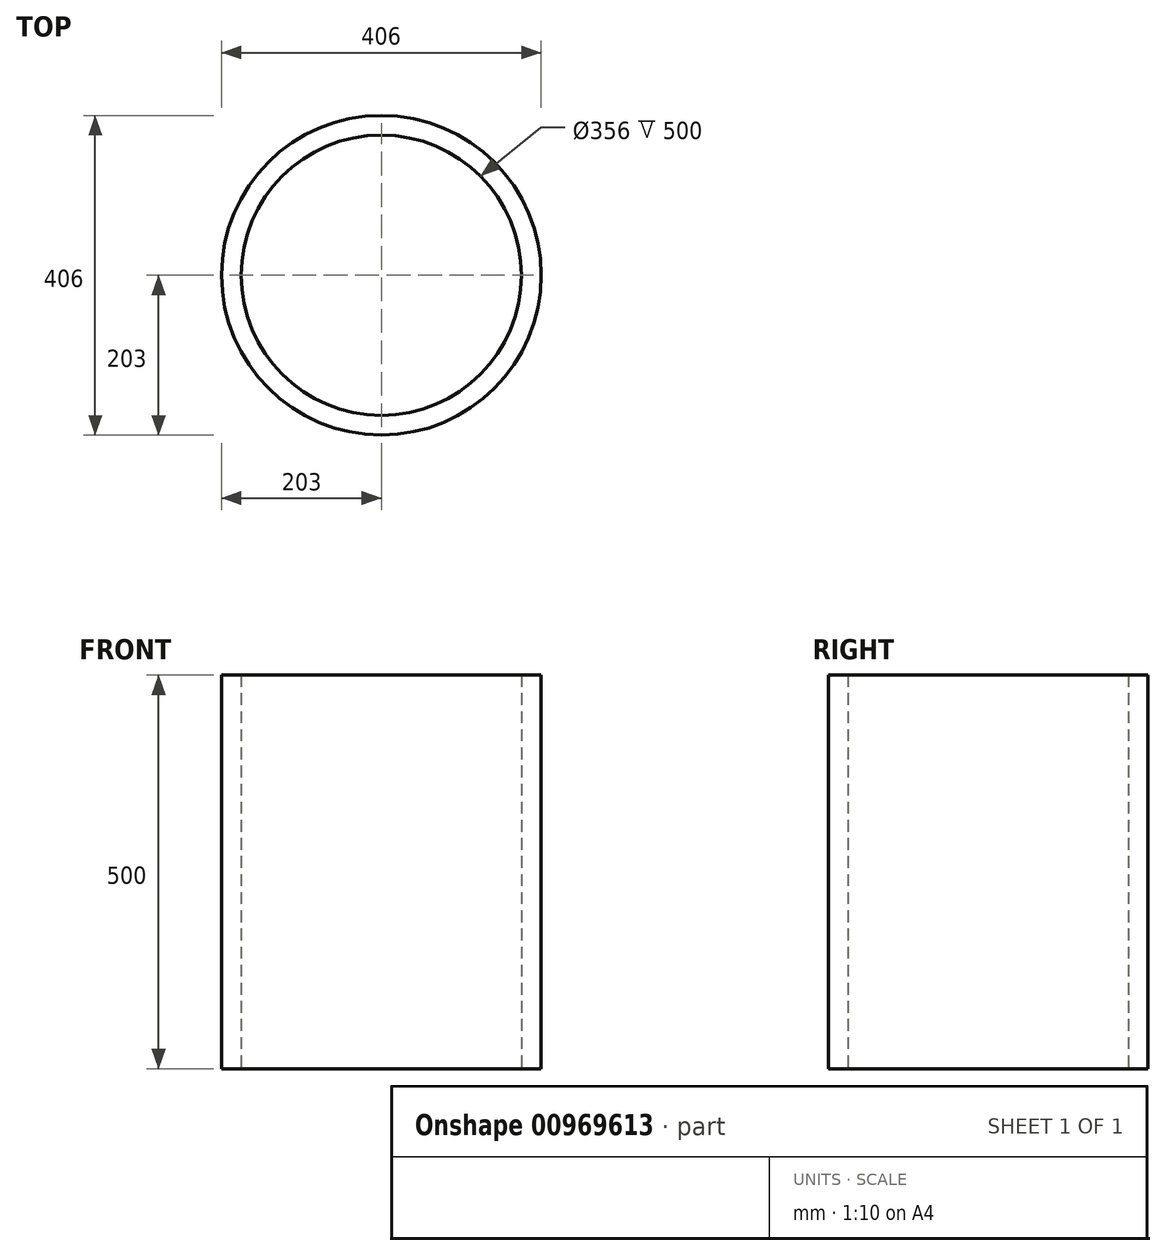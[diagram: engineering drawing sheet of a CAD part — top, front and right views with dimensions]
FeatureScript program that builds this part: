
annotation { "Feature Type Name" : "Feature", "Feature Type Description" : "" }
export const myFeature = defineFeature(function(context is Context, id is Id, definition is map)
    precondition{}
    {
        {
            var Q0;
            Q0=qCreatedBy(makeId("Top.planeOp"),FACE);
            var sketch = newSketch(context, id + "F0", { "sketchPlane" : qUnion([Q0])});
            skCircle(sketch, "E0", {"center": v(0, 0) * mm, "radius": 203 * mm});
            skCircle(sketch, "E1", {"center": v(0, 0) * mm, "radius": 178 * mm});
            skSolve(sketch);
        }
        {
            var Q0;
            Q0 = qSketchRegion(id + "F0", true);
            extrude(context, id + "F1", {"entities" : qUnion([Q0]), "depth" : 500 * mm, "offsetDistance" : 25 * mm});
        }
    });
